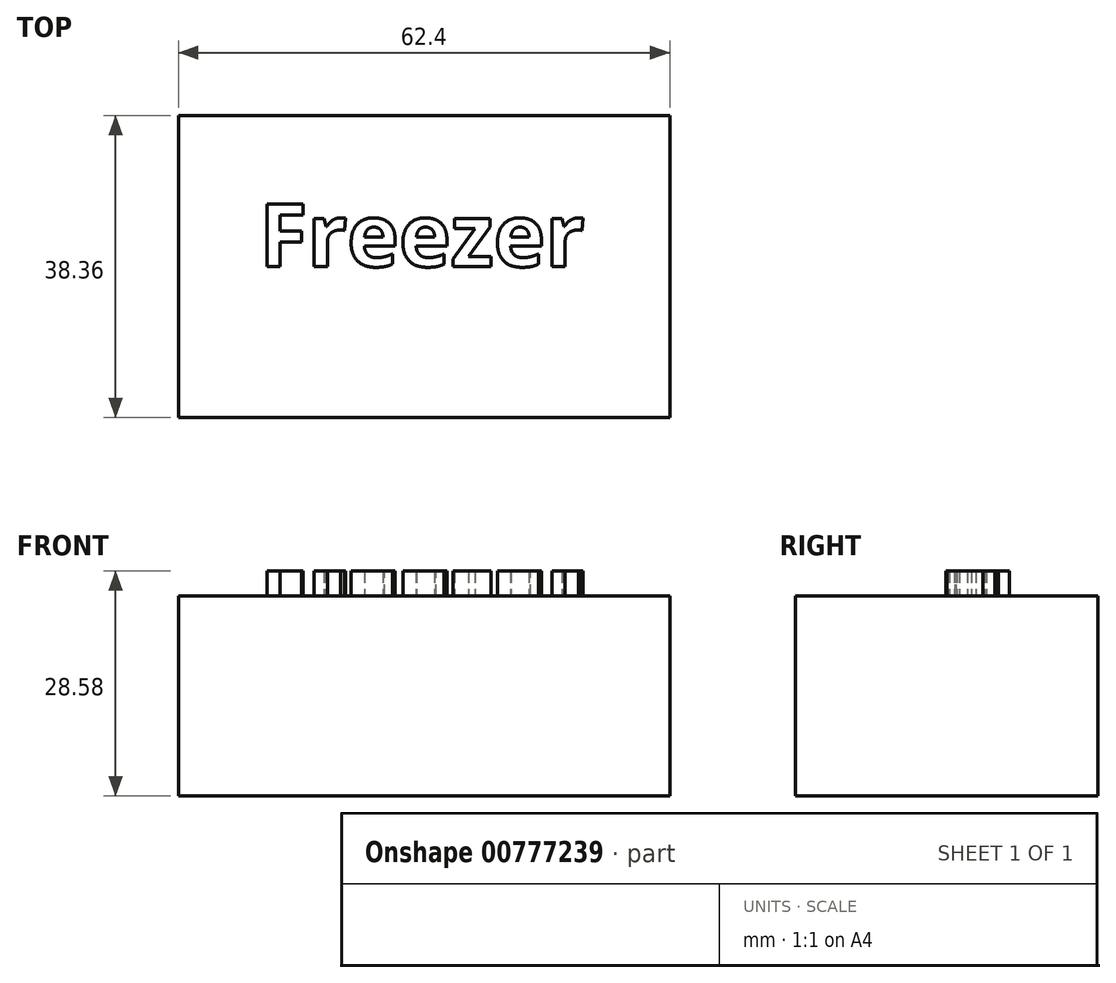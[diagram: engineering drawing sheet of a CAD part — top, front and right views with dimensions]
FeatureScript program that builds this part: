
annotation { "Feature Type Name" : "Feature", "Feature Type Description" : "" }
export const myFeature = defineFeature(function(context is Context, id is Id, definition is map)
    precondition{}
    {
        {
            var Q0;
            Q0=qCreatedBy(makeId("Top.planeOp"),FACE);
            var sketch = newSketch(context, id + "F0", { "sketchPlane" : qUnion([Q0])});
            skLineSegment(sketch, "E0.bottom", {"start": v(-31.2, 19.18) * mm, "end": v(31.2, 19.18) * mm});
            skLineSegment(sketch, "E0.top", {"start": v(-31.2, -19.18) * mm, "end": v(31.2, -19.18) * mm});
            skLineSegment(sketch, "E0.left", {"start": v(-31.2, 19.18) * mm, "end": v(-31.2, -19.18) * mm});
            skLineSegment(sketch, "E0.right", {"start": v(31.2, 19.18) * mm, "end": v(31.2, -19.18) * mm});
            skPoint(sketch, "E0.middle", {"position": v(0, 0) * mm});
            skSolve(sketch);
        }
        {
            var Q0;
            Q0=makeQuery(id+"F0.imprint","IMPRINT",FACE,{"disambiguationData":[TD([[makeQuery(id+"F0.imprint","IMPRINT",EDGE,{"derivedFrom":sQuery(id+"F0.wireOp",EDGE,"E0.bottom")}),-1.0]])]});
            extrude(context, id + "F1", {"entities" : qUnion([Q0]), "depth" : 25.4 * mm, "offsetDistance" : 25.4 * mm});
        }
        {
            var Q0;
            Q0=makeQuery(id+"F1.opExtrude","CAP_FACE",FACE,{"disambiguationData":[OSD([sQuery(id+"F0.wireOp",EDGE,"E0.bottom"),sQuery(id+"F0.wireOp",EDGE,"E0.top"),sQuery(id+"F0.wireOp",EDGE,"E0.left"),sQuery(id+"F0.wireOp",EDGE,"E0.right")])],"isStart":false});
            var sketch = newSketch(context, id + "F2", { "sketchPlane" : qUnion([Q0])});
            skText(sketch, "E1", { "text": "Freezer", "fontName": "OpenSans-Bold.ttf"});
            const initialGuessF2  = {"E1": [-0.02093, 0, 1, 0, 0.00801]};
            skSetInitialGuess(sketch, initialGuessF2);
            skSolve(sketch);
        }
        {
            var Q0;
            Q0 = qSketchRegion(id + "F2", true);
            extrude(context, id + "F3", {"entities" : qUnion([Q0]), "operationType" : NewBodyOperationType.ADD, "depth" : 3.17 * mm, "offsetDistance" : 25.4 * mm});
        }
    });
